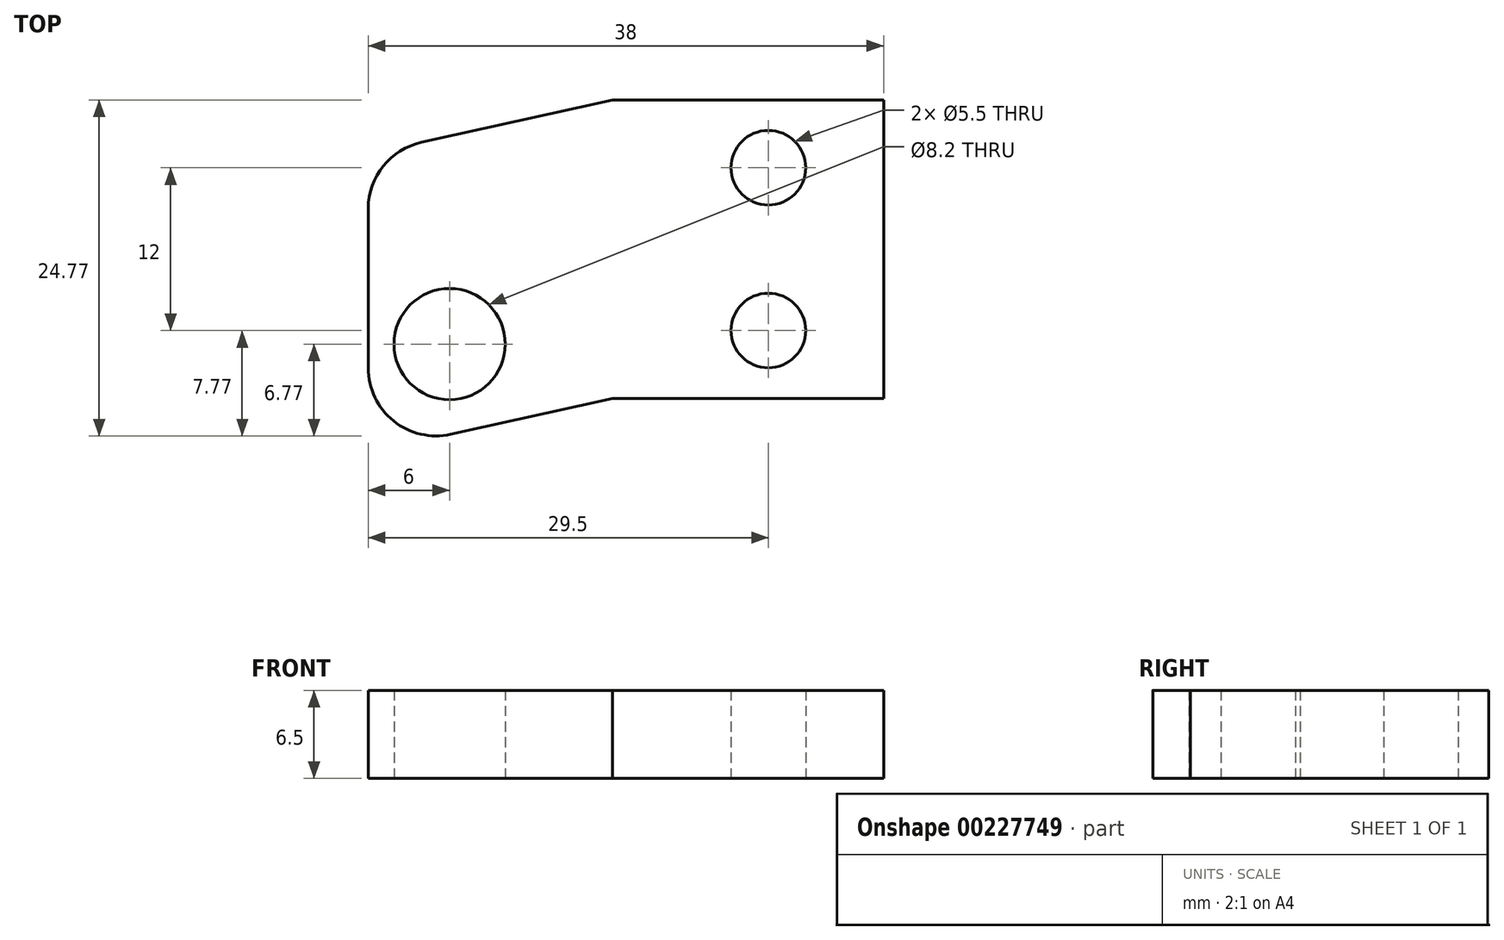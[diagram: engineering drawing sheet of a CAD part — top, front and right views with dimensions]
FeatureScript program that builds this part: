
annotation { "Feature Type Name" : "Feature", "Feature Type Description" : "" }
export const myFeature = defineFeature(function(context is Context, id is Id, definition is map)
    precondition{}
    {
        {
            var Q0;
            Q0=qCreatedBy(makeId("Top.planeOp"),FACE);
            var sketch = newSketch(context, id + "F0", { "sketchPlane" : qUnion([Q0])});
            skLineSegment(sketch, "E0.left", {"start": v(0, 18) * mm, "end": v(0, 0) * mm});
            skLineSegment(sketch, "E0.right", {"start": v(38, 22) * mm, "end": v(38, 0) * mm});
            skCircle(sketch, "E1", {"center": v(6, 4) * mm, "radius": 4.1 * mm});
            skPoint(sketch, "E1.centerSnap0", {"position": v(0, 9) * mm});
            skPoint(sketch, "E2", {"position": v(29.5, 17) * mm});
            skPoint(sketch, "E3", {"position": v(29.5, 5) * mm});
            skLineSegment(sketch, "E4", {"start": v(18, 22) * mm, "end": v(18, 0) * mm, "construction": true});
            skLineSegment(sketch, "E5", {"start": v(18, 0) * mm, "end": v(0, -4) * mm});
            skLineSegment(sketch, "E6", {"start": v(0, -4) * mm, "end": v(0, 0) * mm});
            skLineSegment(sketch, "E7.trimOffspring", {"start": v(18, 0) * mm, "end": v(38, 0) * mm});
            skLineSegment(sketch, "E8", {"start": v(0, 18) * mm, "end": v(18, 22) * mm});
            skLineSegment(sketch, "E9", {"start": v(38, 22) * mm, "end": v(18, 22) * mm});
            skLineSegment(sketch, "E10", {"start": v(29.5, 17) * mm, "end": v(29.5, 5) * mm, "construction": true});
            skPoint(sketch, "E11", {"position": v(29.5, 11) * mm});
            skSolve(sketch);
        }
        {
            var Q0;
            Q0 = qSketchRegion(id + "F0", true);
            extrude(context, id + "F1", {"entities" : qUnion([Q0]), "depth" : 6.5 * mm, "offsetDistance" : 25 * mm});
        }
        {
            var Q0;
            Q0=sQuery(id+"F0.wireOp",VERTEX,"E2");
            var Q1;
            Q1=sQuery(id+"F0.wireOp",VERTEX,"E3");
            var Q2;
            Q2=makeQuery(id+"F1.opExtrude","SWEPT_BODY",BODY,{"disambiguationData":[OSD([sQuery(id+"F0.wireOp",EDGE,"E0.bottom"),sQuery(id+"F0.wireOp",EDGE,"E0.top"),sQuery(id+"F0.wireOp",EDGE,"E0.left"),sQuery(id+"F0.wireOp",EDGE,"E0.right"),sQuery(id+"F0.wireOp",EDGE,"E1")])]});
            hole(context, id + "F2", {"style" : HoleStyle.SIMPLE, "endStyle" : HoleEndStyle.THROUGH, "oppositeDirection" : true, "standardTappedOrClearance" : lookupTablePath({ "fit" : "Normal", "standard" : "ISO", "size" : "M5", "type" : "Clearance" }), "standardBlindInLast" : lookupTablePath({ "fit" : "Normal", "standard" : "ISO", "engagement" : "75%", "pitch" : "0.8 mm", "size" : "M5", "type" : "Clearance & tapped" }), "holeDiameter" : 5.5 * mm, "majorDiameter" : 5 * mm, "isTappedThrough" : true, "tappedDepth" : 12 * mm, "tapClearance" : 3, "locations" : qUnion([Q0, Q1]), "scope" : qUnion([Q2])});
        }
        {
            var Q0;
            Q0=makeQuery(id+"F1.opExtrude","SWEPT_EDGE",EDGE,{"disambiguationData":[OSD([sQuery(id+"F0.wireOp",EDGE,"E0.bottom"),sQuery(id+"F0.wireOp",EDGE,"E0.left")])]});
            var Q1;
            Q1=makeQuery(id+"F1.opExtrude","SWEPT_EDGE",EDGE,{"disambiguationData":[OSD([sQuery(id+"F0.wireOp",EDGE,"E0.top"),sQuery(id+"F0.wireOp",EDGE,"E0.left")])]});
            var Q2;
            Q2=makeQuery(id+"F1.opExtrude","SWEPT_EDGE",EDGE,{"disambiguationData":[OSD([sQuery(id+"F0.wireOp",EDGE,"E5"),sQuery(id+"F0.wireOp",EDGE,"E6")])]});
            fillet(context, id + "F3", {"entities" : qUnion([Q0, Q1, Q2]), "radius" : 5 * mm, "tangentPropagation" : true, "allowEdgeOverflow" : false});
        }
    });
